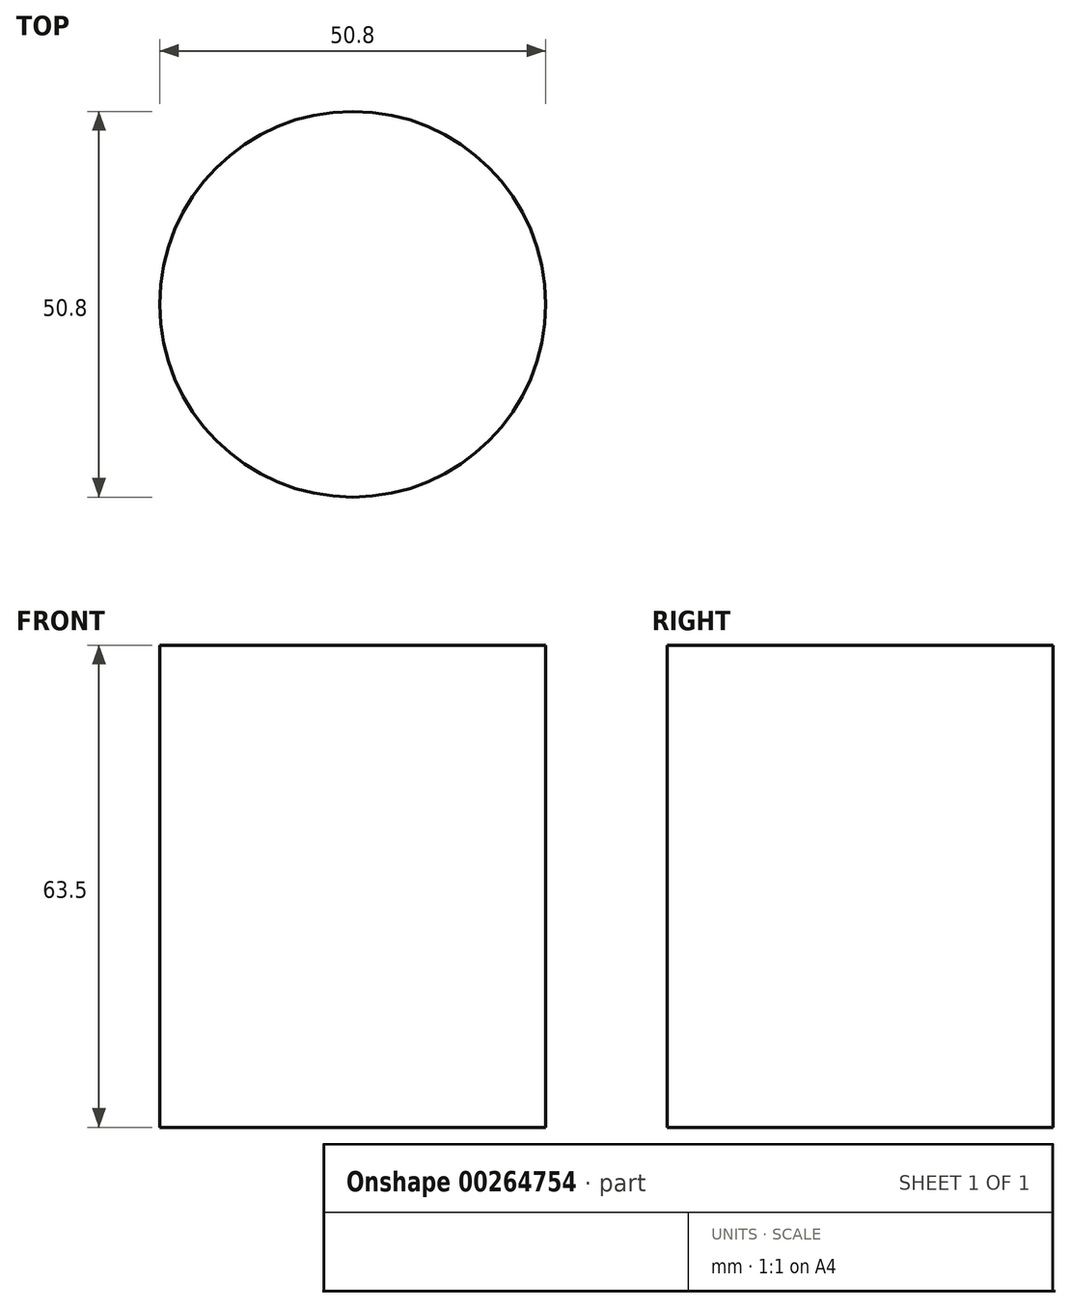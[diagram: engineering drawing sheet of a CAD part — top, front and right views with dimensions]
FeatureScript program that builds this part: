
annotation { "Feature Type Name" : "Feature", "Feature Type Description" : "" }
export const myFeature = defineFeature(function(context is Context, id is Id, definition is map)
    precondition{}
    {
        {
            var Q0;
            Q0=qCreatedBy(makeId("Top.planeOp"),FACE);
            var sketch = newSketch(context, id + "F0", { "sketchPlane" : qUnion([Q0])});
            skCircle(sketch, "E0", {"center": v(0, 0) * mm, "radius": 25.4 * mm});
            skSolve(sketch);
        }
        {
            var Q0;
            Q0 = qSketchRegion(id + "F0", true);
            extrude(context, id + "F1", {"entities" : qUnion([Q0]), "depth" : 63.5 * mm});
        }
    });
